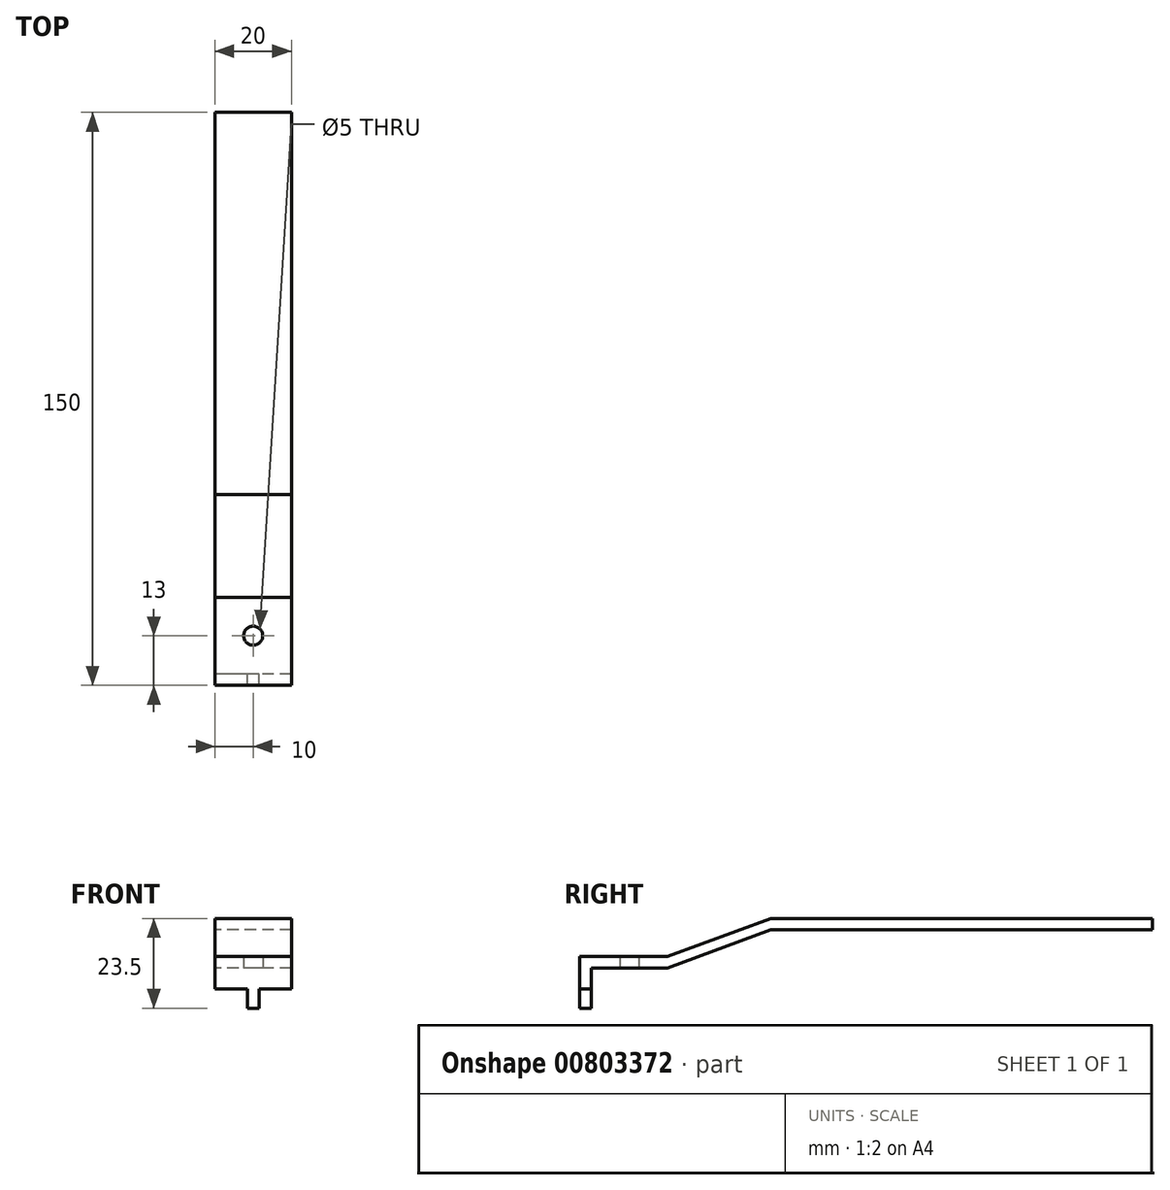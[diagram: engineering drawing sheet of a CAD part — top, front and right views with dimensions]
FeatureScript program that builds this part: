
annotation { "Feature Type Name" : "Feature", "Feature Type Description" : "" }
export const myFeature = defineFeature(function(context is Context, id is Id, definition is map)
    precondition{}
    {
        {
            var Q0;
            Q0=qCreatedBy(makeId("Right.planeOp"),FACE);
            var sketch = newSketch(context, id + "F0", { "sketchPlane" : qUnion([Q0])});
            skLineSegment(sketch, "E0", {"start": v(9.46, 13.92) * mm, "end": v(29.46, 13.92) * mm});
            skLineSegment(sketch, "E1", {"start": v(29.46, 13.92) * mm, "end": v(56.46, 23.92) * mm});
            skLineSegment(sketch, "E2", {"start": v(56.46, 23.92) * mm, "end": v(156.46, 23.92) * mm});
            skLineSegment(sketch, "E3", {"start": v(156.46, 23.92) * mm, "end": v(156.46, 26.92) * mm});
            skLineSegment(sketch, "E4", {"start": v(156.46, 26.92) * mm, "end": v(56.46, 26.92) * mm});
            skLineSegment(sketch, "E5", {"start": v(56.46, 26.92) * mm, "end": v(29.46, 16.92) * mm});
            skLineSegment(sketch, "E6", {"start": v(29.46, 16.92) * mm, "end": v(6.46, 16.92) * mm});
            skLineSegment(sketch, "E7", {"start": v(6.46, 16.92) * mm, "end": v(6.46, 8.42) * mm});
            skLineSegment(sketch, "E8", {"start": v(6.46, 8.42) * mm, "end": v(9.46, 8.42) * mm});
            skLineSegment(sketch, "E9", {"start": v(9.46, 8.42) * mm, "end": v(9.46, 13.92) * mm});
            skSolve(sketch);
        }
        {
            var Q0;
            Q0=makeQuery(id+"F0.imprint","IMPRINT",FACE,{"disambiguationData":[TD([[makeQuery(id+"F0.imprint","IMPRINT",EDGE,{"derivedFrom":sQuery(id+"F0.wireOp",EDGE,"E0")}),1.0]])]});
            extrude(context, id + "F1", {"entities" : qUnion([Q0]), "endBound" : BoundingType.SYMMETRIC, "depth" : 20 * mm, "offsetDistance" : 25 * mm});
        }
        {
            var Q0;
            Q0=qCreatedBy(makeId("Top.planeOp"),FACE);
            var sketch = newSketch(context, id + "F2", { "sketchPlane" : qUnion([Q0])});
            skCircle(sketch, "E10", {"center": v(0, 19.46) * mm, "radius": 2.5 * mm});
            skSolve(sketch);
        }
        {
            var Q0;
            Q0=makeQuery(id+"F2.imprint","IMPRINT",FACE,{"disambiguationData":[TD([[makeQuery(id+"F2.imprint","IMPRINT",EDGE,{"derivedFrom":sQuery(id+"F2.wireOp",EDGE,"E10")}),1.0]])]});
            extrude(context, id + "F3", {"entities" : qUnion([Q0]), "operationType" : NewBodyOperationType.REMOVE, "endBound" : BoundingType.THROUGH_ALL, "depth" : 25 * mm, "offsetDistance" : 25 * mm});
        }
        {
            var Q0;
            Q0=makeQuery(id+"F1.opExtrude","SWEPT_FACE",FACE,{"disambiguationData":[OSD([sQuery(id+"F0.wireOp",EDGE,"E8")])]});
            var sketch = newSketch(context, id + "F4", { "sketchPlane" : qUnion([Q0])});
            skLineSegment(sketch, "E11.bottom", {"start": v(-1.5, -6.46) * mm, "end": v(1.5, -6.46) * mm});
            skLineSegment(sketch, "E11.top", {"start": v(-1.5, -9.46) * mm, "end": v(1.5, -9.46) * mm});
            skLineSegment(sketch, "E11.left", {"start": v(-1.5, -6.46) * mm, "end": v(-1.5, -9.46) * mm});
            skLineSegment(sketch, "E11.right", {"start": v(1.5, -6.46) * mm, "end": v(1.5, -9.46) * mm});
            skSolve(sketch);
        }
        {
            var Q0;
            Q0=makeQuery(id+"F4.imprint","IMPRINT",FACE,{"disambiguationData":[TD([[makeQuery(id+"F4.imprint","IMPRINT",EDGE,{"derivedFrom":sQuery(id+"F4.wireOp",EDGE,"E11.bottom")}),1.0]])]});
            extrude(context, id + "F5", {"entities" : qUnion([Q0]), "operationType" : NewBodyOperationType.ADD, "depth" : 5 * mm, "offsetDistance" : 25 * mm});
        }
    });
